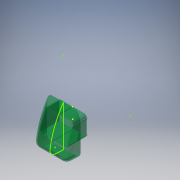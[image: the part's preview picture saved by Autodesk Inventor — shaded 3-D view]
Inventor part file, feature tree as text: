
AUTODESK INVENTOR PART (.ipt)
format: ipt  version: 2018 (Build 220112000, 112)  size: 485,376 bytes
history: native  units: in
note: dims shown in document units (in); Inventor stores cm internally (conversion verified against a paired STEP export)
features: sketch x8, extrude x6, fillet x2, shell x2, plane x1
ambient origin geometry x8: Origin, YZ Plane, XZ Plane, XY Plane, X Axis, Y Axis, Z Axis, Center Point
bodies: Solid1 (feature_tree)
feature tree (19):
  plane  "Work Plane1"
  extrude  "Extrusion1"  Depth=2.55in TaperAngle=0.0deg
  fillet  "Fillet1"  Radius=0.5in
  shell  "Shell1"  Thickness=0.07in
  sketch  "Sketch3"  dims[d3=-0.0175in d11=2.55in d12=0.0in d13=0.5in d14=0.07in]
  sketch  "Sketch4"  dims[d33=1.5in d36=0.0in d37=0.0in d38=0.1in d39=0.2in]
  sketch  "Sketch5"  dims[d40=0.05in d41=0.05in]
  extrude  "Extrusion4"  TaperAngle=0.0deg  [1 undecoded]
  shell  "Shell3"  Thickness=0.1in
  fillet  "Fillet3"  Radius=0.2in
  sketch  "Sketch6"  dims[d42=0.0in d43=0.0in d51=0.05in d52=0.05in d54=0.0in d55=0.0in]
  extrude  "Extrusion5"  Depth=0.05in
  extrude  "Extrusion8"  Depth=0.05in TaperAngle=0.0deg
  sketch  "Sketch7"  dims[d56=0.05in d57=90.0deg]
  sketch  "Sketch11"  dims[d60=0.05in]
  sketch  "Sketch10"  dims[d58=0.05in d59=90.0deg]
  sketch  "Sketch12"  dims[d63=1.0in d64=0.0in d67=0.05in d68=0.05in d69=0.05in d71=0.0in d72=1.0in d76=0.05in d77=90.0deg d78=0.05in d79=0.0in]
  extrude  "Extrusion7"  TaperAngle=90.0deg  [1 undecoded]
  extrude  "Extrusion9"  TaperAngle=90.0deg  [1 undecoded]
note: 3 required parameter values undecoded (feature->parameter linkage not recoverable at this tier; creation-order binding heuristic only, values carry confidence <= 0.55)
